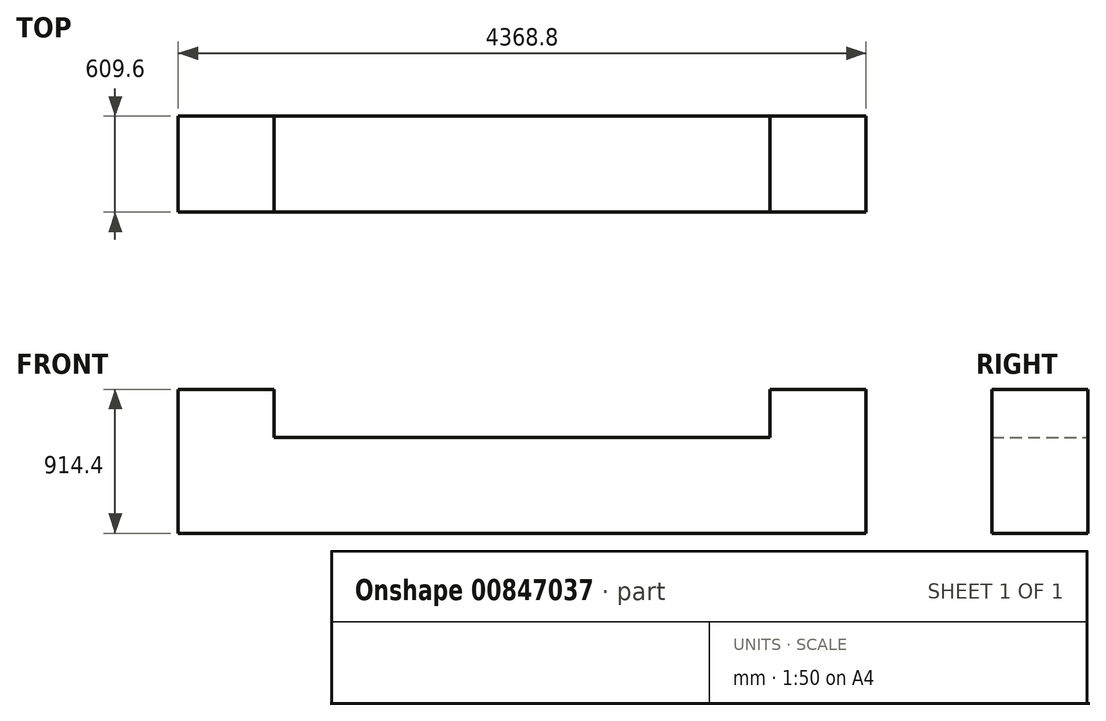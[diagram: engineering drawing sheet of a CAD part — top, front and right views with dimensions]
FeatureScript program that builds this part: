
annotation { "Feature Type Name" : "Feature", "Feature Type Description" : "" }
export const myFeature = defineFeature(function(context is Context, id is Id, definition is map)
    precondition{}
    {
        {
            var Q0;
            Q0=qCreatedBy(makeId("Front.planeOp"),FACE);
            var sketch = newSketch(context, id + "F0", { "sketchPlane" : qUnion([Q0])});
            skLineSegment(sketch, "E0", {"start": v(0, 0) * mm, "end": v(4368.8, 0) * mm});
            skLineSegment(sketch, "E1", {"start": v(4368.8, 0) * mm, "end": v(4368.8, 914.4) * mm});
            skLineSegment(sketch, "E2", {"start": v(4368.8, 914.4) * mm, "end": v(3759.2, 914.4) * mm});
            skLineSegment(sketch, "E3", {"start": v(3759.2, 914.4) * mm, "end": v(3759.2, 609.6) * mm});
            skLineSegment(sketch, "E4", {"start": v(3759.2, 609.6) * mm, "end": v(609.6, 609.6) * mm});
            skLineSegment(sketch, "E5", {"start": v(609.6, 609.6) * mm, "end": v(609.6, 914.4) * mm});
            skLineSegment(sketch, "E6", {"start": v(609.6, 914.4) * mm, "end": v(0, 914.4) * mm});
            skLineSegment(sketch, "E7", {"start": v(0, 914.4) * mm, "end": v(0, 0) * mm});
            skSolve(sketch);
        }
        {
            var Q0;
            Q0 = qSketchRegion(id + "F0", true);
            extrude(context, id + "F1", {"entities" : qUnion([Q0]), "depth" : 609.6 * mm, "offsetDistance" : 25.4 * mm});
        }
    });
